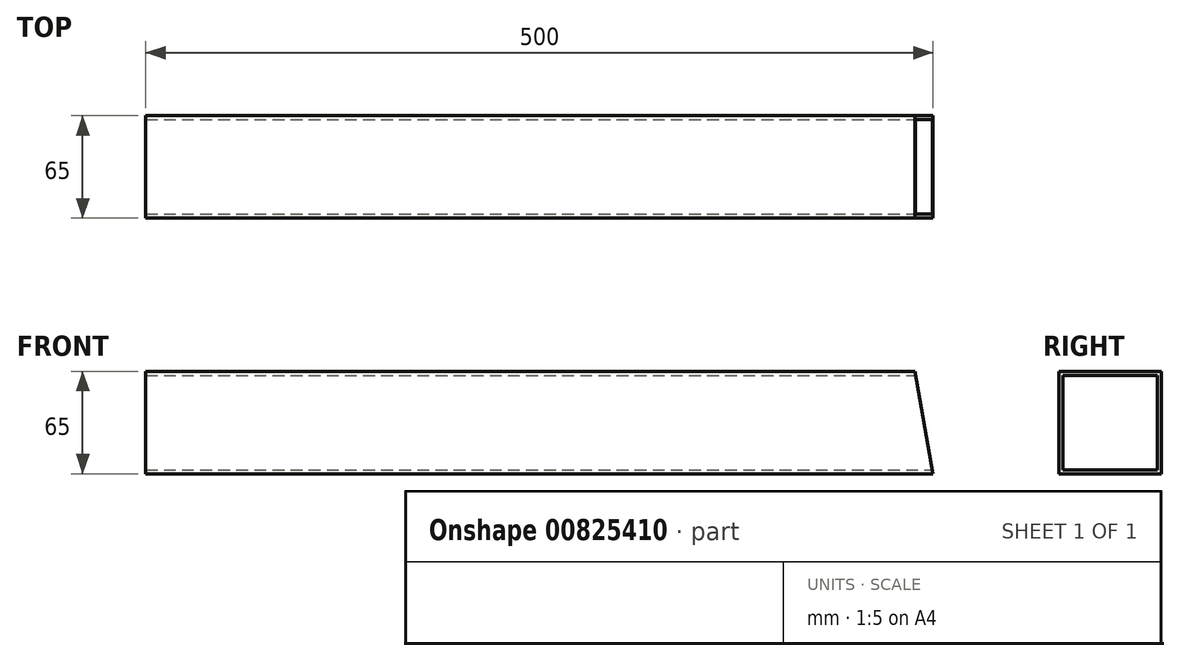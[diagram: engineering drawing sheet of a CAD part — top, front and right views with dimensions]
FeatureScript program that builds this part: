
annotation { "Feature Type Name" : "Feature", "Feature Type Description" : "" }
export const myFeature = defineFeature(function(context is Context, id is Id, definition is map)
    precondition{}
    {
        {
            var Q0;
            Q0=qCreatedBy(makeId("Right.planeOp"),FACE);
            var sketch = newSketch(context, id + "F0", { "sketchPlane" : qUnion([Q0])});
            skLineSegment(sketch, "E0.bottom", {"start": v(-7.37, 14.87) * mm, "end": v(57.63, 14.87) * mm});
            skLineSegment(sketch, "E0.top", {"start": v(-7.37, -50.13) * mm, "end": v(57.63, -50.13) * mm});
            skLineSegment(sketch, "E0.left", {"start": v(-7.37, 14.87) * mm, "end": v(-7.37, -50.13) * mm});
            skLineSegment(sketch, "E0.right", {"start": v(57.63, 14.87) * mm, "end": v(57.63, -50.13) * mm});
            skSolve(sketch);
        }
        {
            var Q0;
            Q0=makeQuery(id+"F0.imprint","IMPRINT",FACE,{"disambiguationData":[TD([[makeQuery(id+"F0.imprint","IMPRINT",EDGE,{"derivedFrom":sQuery(id+"F0.wireOp",EDGE,"E0.bottom")}),-1.0]])]});
            extrude(context, id + "F1", {"entities" : qUnion([Q0]), "depth" : 500 * mm, "offsetDistance" : 25 * mm});
        }
        {
            var Q0;
            Q0=makeQuery(id+"F1.opExtrude","CAP_FACE",FACE,{"disambiguationData":[OSD([sQuery(id+"F0.wireOp",EDGE,"E0.bottom"),sQuery(id+"F0.wireOp",EDGE,"E0.top"),sQuery(id+"F0.wireOp",EDGE,"E0.left"),sQuery(id+"F0.wireOp",EDGE,"E0.right")])],"isStart":false});
            var sketch = newSketch(context, id + "F2", { "sketchPlane" : qUnion([Q0])});
            skLineSegment(sketch, "E1.bottom", {"start": v(-4.87, 12.37) * mm, "end": v(55.13, 12.37) * mm});
            skLineSegment(sketch, "E1.top", {"start": v(-4.87, -47.63) * mm, "end": v(55.13, -47.63) * mm});
            skLineSegment(sketch, "E1.left", {"start": v(-4.87, 12.37) * mm, "end": v(-4.87, -47.63) * mm});
            skLineSegment(sketch, "E1.right", {"start": v(55.13, 12.37) * mm, "end": v(55.13, -47.63) * mm});
            skSolve(sketch);
        }
        {
            var Q0;
            Q0=makeQuery(id+"F2.imprint","IMPRINT",FACE,{"disambiguationData":[TD([[makeQuery(id+"F2.imprint","IMPRINT",EDGE,{"derivedFrom":sQuery(id+"F2.wireOp",EDGE,"E1.bottom")}),-1.0]])]});
            extrude(context, id + "F3", {"entities" : qUnion([Q0]), "operationType" : NewBodyOperationType.REMOVE, "oppositeDirection" : true, "depth" : 500 * mm, "offsetDistance" : 25 * mm});
        }
        {
            var Q0;
            Q0=makeQuery(id+"F1.opExtrude","SWEPT_FACE",FACE,{"disambiguationData":[OSD([sQuery(id+"F0.wireOp",EDGE,"E0.left")])]});
            var sketch = newSketch(context, id + "F4", { "sketchPlane" : qUnion([Q0])});
            skLineSegment(sketch, "E2", {"start": v(500, -50.13) * mm, "end": v(500, 14.87) * mm});
            skLineSegment(sketch, "E3", {"start": v(500, 14.87) * mm, "end": v(488.54, 14.87) * mm});
            skLineSegment(sketch, "E4", {"start": v(488.54, 14.87) * mm, "end": v(500, -50.13) * mm});
            skSolve(sketch);
        }
        {
            var Q0;
            Q0=makeQuery(id+"F4.imprint","IMPRINT",FACE,{"disambiguationData":[TD([[makeQuery(id+"F4.imprint","IMPRINT",EDGE,{"derivedFrom":sQuery(id+"F4.wireOp",EDGE,"E2")}),-1.0]])]});
            extrude(context, id + "F5", {"entities" : qUnion([Q0]), "operationType" : NewBodyOperationType.REMOVE, "oppositeDirection" : true, "depth" : 70 * mm, "offsetDistance" : 25 * mm});
        }
    });
